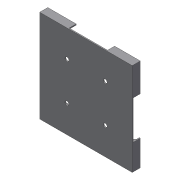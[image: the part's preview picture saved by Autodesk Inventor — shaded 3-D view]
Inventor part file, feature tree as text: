
AUTODESK INVENTOR PART (.ipt)
format: ipt  version: 2017 (Build 210142000, 142)  size: 193,536 bytes
history: native  units: mm
features: sketch x5, extrude x3, projected_geometry x3, hole x1, pattern_circular x1
ambient origin geometry x8: Origin, YZ Plane, XZ Plane, XY Plane, X Axis, Y Axis, Z Axis, Center Point
bodies: Solid1 (feature_tree)
feature tree (13):
  extrude  "Extrusion1"  Depth=90.0mm
  sketch  "Sketch2"  dims[d2=92.0mm d3=92.0mm]
  extrude  "Extrusion2"  Depth=92.0mm
  extrude  "Extrusion3"  Depth=90.0mm
  hole  "Hole1"  [1 undecoded]
  pattern_circular  "Circular Pattern2"  [2 undecoded]
  sketch  "Sketch1"  dims[d0=90.0mm d1=90.0mm]
  projected_geometry  "Projected Loop1"
  sketch  "Sketch3"  dims[d4=1.0mm d5=0.0mm d6=90.0mm]
  sketch  "Sketch4"  dims[d7=90.0mm d8=1.0mm]
  projected_geometry  "Projected Loop2"
  projected_geometry  "Projected Loop3"
  sketch  "Sketch5"  dims[d9=1.0mm d10=10.0mm d11=10.0mm d12=14.5mm d13=17.25mm d14=7.0mm d15=0.0mm d16=22.5mm d17=8.625mm d18=10.0mm d19=0.0mm d23=27.0mm d24=27.0mm d25=4.0mm d26=6.0mm d27=4.0mm d28=2.0mm d29=90.0deg d30=8.0mm d31=20.594885mm d32=40.0mm d33=360.0deg]
note: 3 required parameter values undecoded (feature->parameter linkage not recoverable at this tier; creation-order binding heuristic only, values carry confidence <= 0.55)
